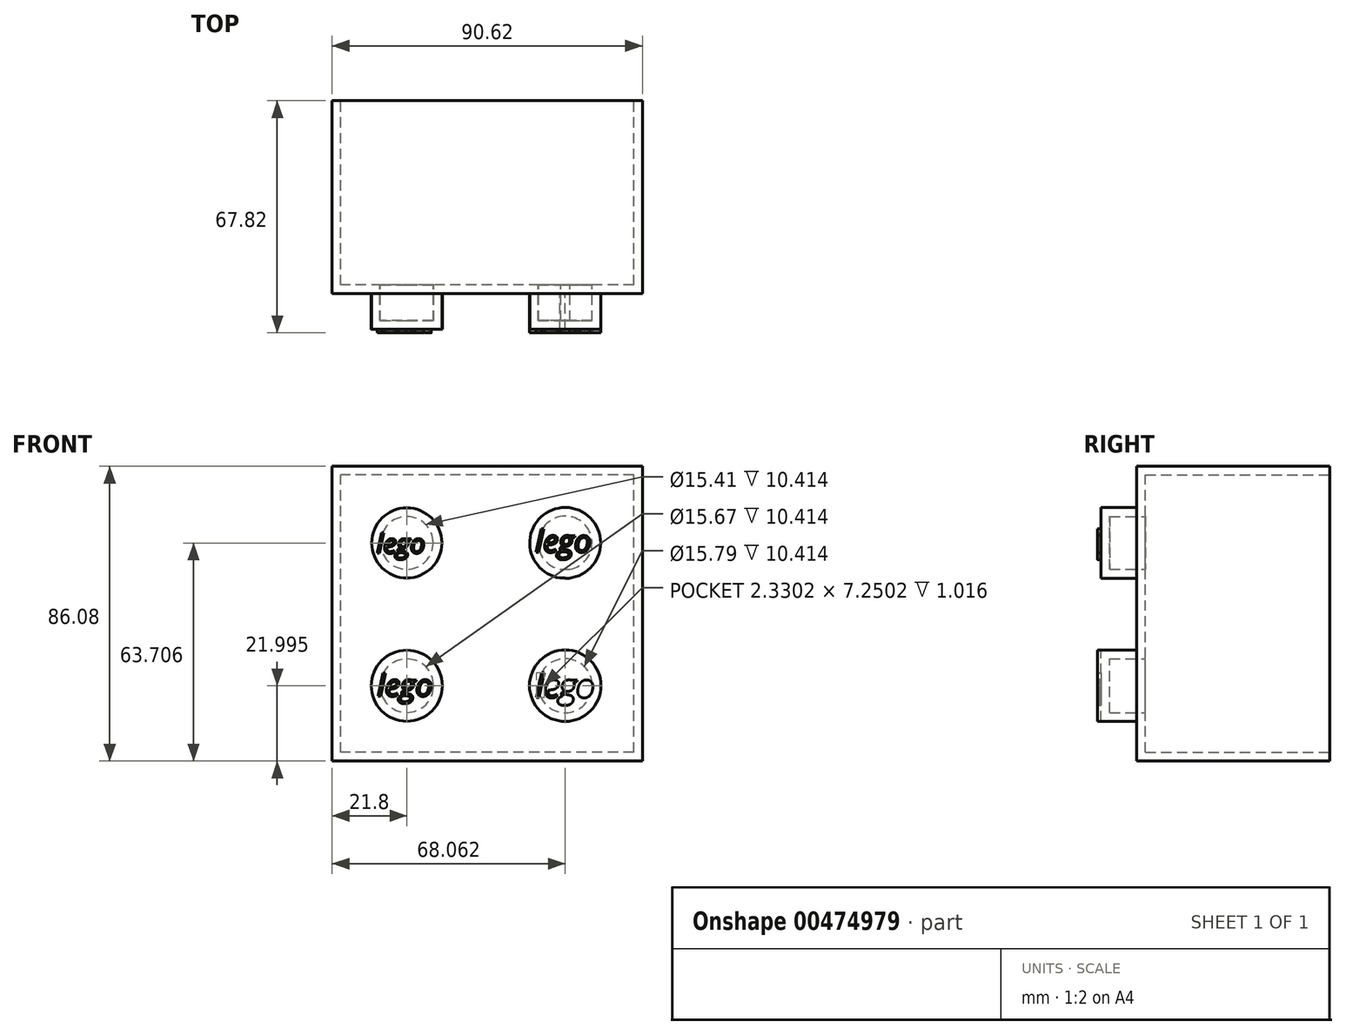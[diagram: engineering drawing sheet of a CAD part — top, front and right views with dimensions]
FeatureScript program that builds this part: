
annotation { "Feature Type Name" : "Feature", "Feature Type Description" : "" }
export const myFeature = defineFeature(function(context is Context, id is Id, definition is map)
    precondition{}
    {
        {
            var Q0;
            Q0=qCreatedBy(makeId("Front.planeOp"),FACE);
            var sketch = newSketch(context, id + "F0", { "sketchPlane" : qUnion([Q0])});
            skLineSegment(sketch, "E0.bottom", {"start": v(45.31, -43.04) * mm, "end": v(-45.31, -43.04) * mm});
            skLineSegment(sketch, "E0.top", {"start": v(45.31, 43.04) * mm, "end": v(-45.31, 43.04) * mm});
            skLineSegment(sketch, "E0.left", {"start": v(45.31, -43.04) * mm, "end": v(45.31, 43.04) * mm});
            skLineSegment(sketch, "E0.right", {"start": v(-45.31, -43.04) * mm, "end": v(-45.31, 43.04) * mm});
            skPoint(sketch, "E0.middle", {"position": v(0, 0) * mm});
            skSolve(sketch);
        }
        {
            var Q0;
            Q0=makeQuery(id+"F0.imprint","IMPRINT",FACE,{"disambiguationData":[TD([[makeQuery(id+"F0.imprint","IMPRINT",EDGE,{"derivedFrom":sQuery(id+"F0.wireOp",EDGE,"E0.bottom")}),-1.0]])]});
            extrude(context, id + "F1", {"entities" : qUnion([Q0]), "depth" : 56.4 * mm});
        }
        {
            var Q0;
            Q0=makeQuery(id+"F1.opExtrude","CAP_FACE",FACE,{"disambiguationData":[OSD([sQuery(id+"F0.wireOp",EDGE,"E0.bottom"),sQuery(id+"F0.wireOp",EDGE,"E0.top"),sQuery(id+"F0.wireOp",EDGE,"E0.left"),sQuery(id+"F0.wireOp",EDGE,"E0.right")])],"isStart":false});
            var sketch = newSketch(context, id + "F2", { "sketchPlane" : qUnion([Q0])});
            skCircle(sketch, "E1", {"center": v(-23.51, 20.67) * mm, "radius": 10.25 * mm});
            skArc(sketch, "E2", {"start": v(22.75, 10.3) * mm, "mid": v(23.52, 31) * mm, "end": v(21.21, 10.42) * mm});
            skLineSegment(sketch, "E3", {"start": v(22.7, 31.03) * mm, "end": v(22.75, 31.03) * mm});
            skLineSegment(sketch, "E4", {"start": v(21.21, 10.42) * mm, "end": v(22.75, 10.42) * mm});
            skLineSegment(sketch, "E5", {"start": v(22.75, 10.42) * mm, "end": v(22.75, 10.3) * mm});
            skLineSegment(sketch, "E6", {"start": v(33.18, -20.72) * mm, "end": v(33.18, -21.05) * mm});
            skLineSegment(sketch, "E7", {"start": v(12.4, -19.82) * mm, "end": v(12.4, -21.05) * mm});
            skCircle(sketch, "E8", {"center": v(-23.51, -21.05) * mm, "radius": 10.37 * mm});
            skCircle(sketch, "E9", {"center": v(22.75, -21.05) * mm, "radius": 10.43 * mm});
            skPoint(sketch, "E10.orphan", {"position": v(-33.76, 20.67) * mm});
            skPoint(sketch, "E11.end.orphan", {"position": v(-33.76, -21.05) * mm});
            skPoint(sketch, "E12.trimOffspring.end.orphan", {"position": v(-13.26, -21.05) * mm});
            skPoint(sketch, "E13.orphan", {"position": v(-23.51, 10.42) * mm});
            skPoint(sketch, "E14.orphan", {"position": v(-23.51, 30.91) * mm});
            skSolve(sketch);
        }
        {
            var Q0;
            Q0=makeQuery(id+"F2.imprint","IMPRINT",FACE,{"disambiguationData":[TD([[makeQuery(id+"F2.imprint","IMPRINT",EDGE,{"derivedFrom":sQuery(id+"F2.wireOp",EDGE,"E1")}),1.0]])]});
            var Q1;
            Q1=makeQuery(id+"F2.imprint","IMPRINT",FACE,{"disambiguationData":[TD([[makeQuery(id+"F2.imprint","IMPRINT",EDGE,{"derivedFrom":sQuery(id+"F2.wireOp",EDGE,"E8")}),1.0]])]});
            var Q2;
            {var subQ0=sQuery(id+"F2.wireOp",EDGE,"E9");var subQ1=makeQuery(id+"F2.imprint","IMPRINT",VERTEX,{"disambiguationData":[OD(0.0)],"derivedFrom":subQ0});Q2=makeQuery(id+"F2.imprint","IMPRINT",FACE,{"disambiguationData":[TD([[makeQuery(id+"F2.imprint","IMPRINT",EDGE,{"disambiguationData":[TD([[subQ1,-1.0]])],"derivedFrom":subQ0}),1.0]])]});}
            var Q3;
            {var subQ1=sQuery(id+"F2.wireOp",EDGE,"E3");Q3=makeQuery(id+"F2.imprint","IMPRINT",FACE,{"disambiguationData":[TD([[makeQuery(id+"F2.imprint","IMPRINT",EDGE,{"derivedFrom":subQ1}),-1.0]])]});}
            extrude(context, id + "F3", {"entities" : qUnion([Q0, Q1, Q2, Q3]), "operationType" : NewBodyOperationType.ADD, "depth" : 10.4 * mm});
        }
        {
            var Q0;
            Q0=makeQuery(id+"F1.opExtrude","CAP_FACE",FACE,{"disambiguationData":[OSD([sQuery(id+"F0.wireOp",EDGE,"E0.bottom"),sQuery(id+"F0.wireOp",EDGE,"E0.top"),sQuery(id+"F0.wireOp",EDGE,"E0.left"),sQuery(id+"F0.wireOp",EDGE,"E0.right")])],"isStart":true});
            shell(context, id + "F4", {"entities" : qUnion([Q0]), "thickness" : 2.54 * mm});
        }
        {
            var Q0;
            Q0=makeQuery(id+"F3.opExtrude","CAP_FACE",FACE,{"disambiguationData":[OSD([sQuery(id+"F2.wireOp",EDGE,"E1")])],"isStart":false});
            var sketch = newSketch(context, id + "F5", { "sketchPlane" : qUnion([Q0])});
            skText(sketch, "E15", { "text": "lego\n", "fontName": "OpenSans-Italic.ttf"});
            const initialGuessF5  = {"E15": [-0.03238, 0.01765, 1, 0, 0.00566]};
            skSetInitialGuess(sketch, initialGuessF5);
            skSolve(sketch);
        }
        {
            var Q0;
            Q0=makeQuery(id+"F3.opExtrude","CAP_FACE",FACE,{"disambiguationData":[OSD([sQuery(id+"F2.wireOp",EDGE,"E2"),sQuery(id+"F2.wireOp",EDGE,"E3"),sQuery(id+"F2.wireOp",EDGE,"E4"),sQuery(id+"F2.wireOp",EDGE,"E5")])],"isStart":false});
            var sketch = newSketch(context, id + "F6", { "sketchPlane" : qUnion([Q0])});
            skText(sketch, "E16", { "text": "lego", "fontName": "OpenSans-Italic.ttf"});
            const initialGuessF6  = {"E16": [0.014, 0.01793, 1, 0, 0.00652]};
            skSetInitialGuess(sketch, initialGuessF6);
            skSolve(sketch);
        }
        {
            var Q0;
            Q0=makeQuery(id+"F3.opExtrude","CAP_FACE",FACE,{"disambiguationData":[OSD([sQuery(id+"F2.wireOp",EDGE,"E9")])],"isStart":false});
            var sketch = newSketch(context, id + "F7", { "sketchPlane" : qUnion([Q0])});
            skText(sketch, "E17", { "text": "lego", "fontName": "OpenSans-Italic.ttf"});
            const initialGuessF7  = {"E17": [0.01403, -0.02453, 1, 0, 0.00687]};
            skSetInitialGuess(sketch, initialGuessF7);
            skSolve(sketch);
        }
        {
            var Q0;
            Q0=makeQuery(id+"F3.opExtrude","CAP_FACE",FACE,{"disambiguationData":[OSD([sQuery(id+"F2.wireOp",EDGE,"E8")])],"isStart":false});
            var sketch = newSketch(context, id + "F8", { "sketchPlane" : qUnion([Q0])});
            skText(sketch, "E18", { "text": "lego", "fontName": "OpenSans-Italic.ttf"});
            const initialGuessF8  = {"E18": [-0.03216, -0.02413, 1, 0, 0.00645]};
            skSetInitialGuess(sketch, initialGuessF8);
            skSolve(sketch);
        }
        {
            var Q0;
            Q0 = qSketchRegion(id + "F5", true);
            var Q1;
            Q1 = qSketchRegion(id + "F6", true);
            var Q2;
            Q2=makeQuery(id+"F7.imprint","IMPRINT",FACE,{"disambiguationData":[TD([[makeQuery(id+"F7.imprint","IMPRINT",EDGE,{"derivedFrom":sQuery(id+"F7.wireOp",EDGE,"E17.sketch_text.stroke-0")}),1.0]])]});
            var Q3;
            Q3 = qSketchRegion(id + "F8", true);
            extrude(context, id + "F9", {"entities" : qUnion([Q0, Q1, Q2, Q3]), "operationType" : NewBodyOperationType.ADD, "depth" : 1.02 * mm});
        }
    });
